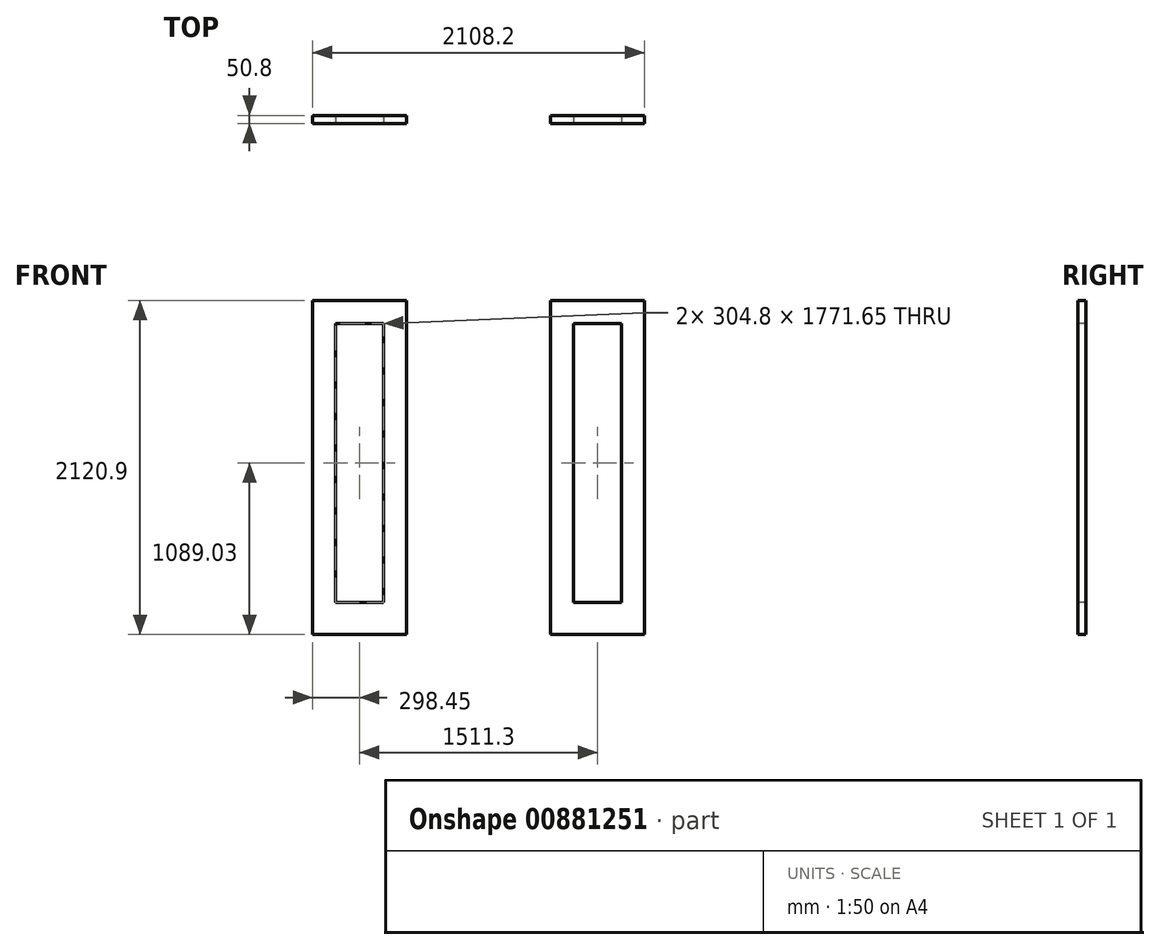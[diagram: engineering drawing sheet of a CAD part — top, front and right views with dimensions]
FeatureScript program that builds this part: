
annotation { "Feature Type Name" : "Feature", "Feature Type Description" : "" }
export const myFeature = defineFeature(function(context is Context, id is Id, definition is map)
    precondition{}
    {
        {
            var Q0;
            Q0=qCreatedBy(makeId("Front.planeOp"),FACE);
            var sketch = newSketch(context, id + "F0", { "sketchPlane" : qUnion([Q0])});
            skLineSegment(sketch, "E0.bottom", {"start": v(-1054.1, 1060.45) * mm, "end": v(1054.1, 1060.45) * mm});
            skLineSegment(sketch, "E0.top", {"start": v(-1054.1, -1060.45) * mm, "end": v(1054.1, -1060.45) * mm});
            skLineSegment(sketch, "E0.left", {"start": v(-1054.1, 1060.45) * mm, "end": v(-1054.1, -1060.45) * mm});
            skLineSegment(sketch, "E0.right", {"start": v(1054.1, 1060.45) * mm, "end": v(1054.1, -1060.45) * mm});
            skSolve(sketch);
        }
        {
            var Q0;
            Q0=qSketchRegion(id+"F0",true);
            extrude(context, id + "F1", {"entities" : qUnion([Q0]), "depth" : 50.8 * mm, "offsetDistance" : 25.4 * mm});
        }
        {
            var Q0;
            Q0=makeQuery(id+"F1.opExtrude","CAP_FACE",FACE,{"disambiguationData":[OSD([sQuery(id+"F0.wireOp",EDGE,"E0.bottom"),sQuery(id+"F0.wireOp",EDGE,"E0.top"),sQuery(id+"F0.wireOp",EDGE,"E0.left"),sQuery(id+"F0.wireOp",EDGE,"E0.right")])],"isStart":false});
            var sketch = newSketch(context, id + "F2", { "sketchPlane" : qUnion([Q0])});
            skLineSegment(sketch, "E1.bottom", {"start": v(-457.2, 1060.45) * mm, "end": v(457.2, 1060.45) * mm});
            skLineSegment(sketch, "E1.top", {"start": v(-457.2, -1060.45) * mm, "end": v(457.2, -1060.45) * mm});
            skLineSegment(sketch, "E1.left", {"start": v(-457.2, 1060.45) * mm, "end": v(-457.2, -1060.45) * mm});
            skLineSegment(sketch, "E1.right", {"start": v(457.2, 1060.45) * mm, "end": v(457.2, -1060.45) * mm});
            skLineSegment(sketch, "E2", {"start": v(-457.2, 0) * mm, "end": v(-1054.1, 0) * mm, "construction": true});
            skLineSegment(sketch, "E3", {"start": v(457.2, 0) * mm, "end": v(1054.1, 0) * mm, "construction": true});
            skSolve(sketch);
        }
        {
            var Q0;
            Q0=qSketchRegion(id+"F2",true);
            extrude(context, id + "F3", {"entities" : qUnion([Q0]), "operationType" : NewBodyOperationType.REMOVE, "oppositeDirection" : true, "depth" : 12.7 * mm, "offsetDistance" : 25.4 * mm});
        }
        {
            var Q0;
            Q0=makeQuery(id+"F3.boolean.opBoolean","COPY",FACE,{"derivedFrom":makeQuery(id+"F3.opExtrude","CAP_FACE",FACE,{"disambiguationData":[OSD([sQuery(id+"F2.wireOp",EDGE,"E1.bottom"),sQuery(id+"F2.wireOp",EDGE,"E1.top"),sQuery(id+"F2.wireOp",EDGE,"E1.left"),sQuery(id+"F2.wireOp",EDGE,"E1.right")])],"isStart":false})});
            var sketch = newSketch(context, id + "F4", { "sketchPlane" : qUnion([Q0])});
            skCircle(sketch, "E4", {"center": v(406.4, 0) * mm, "radius": 25.4 * mm});
            skSolve(sketch);
        }
        {
            var Q0;
            Q0=qSketchRegion(id+"F4",true);
            extrude(context, id + "F5", {"entities" : qUnion([Q0]), "operationType" : NewBodyOperationType.REMOVE, "endBound" : BoundingType.THROUGH_ALL, "oppositeDirection" : true, "depth" : 25.4 * mm, "offsetDistance" : 25.4 * mm});
        }
        {
            var Q0;
            {var subQ0=sQuery(id+"F0.wireOp",EDGE,"E0.bottom");var subQ1=sQuery(id+"F0.wireOp",EDGE,"E0.top");var subQ2=sQuery(id+"F0.wireOp",EDGE,"E0.left");Q0=makeQuery(id+"F3.boolean.opBoolean","SPLIT",FACE,{"disambiguationData":[TD([makeQuery(id+"F1.opExtrude","SWEPT_FACE",FACE,{"disambiguationData":[OSD([subQ2])]})])],"derivedFrom":makeQuery(id+"F1.opExtrude","CAP_FACE",FACE,{"disambiguationData":[OSD([subQ0,subQ1,subQ2,sQuery(id+"F0.wireOp",EDGE,"E0.right")])],"isStart":false})});}
            var sketch = newSketch(context, id + "F6", { "sketchPlane" : qUnion([Q0])});
            skLineSegment(sketch, "E5.bottom", {"start": v(-908.05, 914.4) * mm, "end": v(-603.25, 914.4) * mm});
            skLineSegment(sketch, "E5.top", {"start": v(-908.05, -857.25) * mm, "end": v(-603.25, -857.25) * mm});
            skLineSegment(sketch, "E5.left", {"start": v(-908.05, 914.4) * mm, "end": v(-908.05, -857.25) * mm});
            skLineSegment(sketch, "E5.right", {"start": v(-603.25, 914.4) * mm, "end": v(-603.25, -857.25) * mm});
            skLineSegment(sketch, "E6.bottom", {"start": v(603.25, 914.4) * mm, "end": v(908.05, 914.4) * mm});
            skLineSegment(sketch, "E6.top", {"start": v(603.25, -857.25) * mm, "end": v(908.05, -857.25) * mm});
            skLineSegment(sketch, "E6.left", {"start": v(603.25, 914.4) * mm, "end": v(603.25, -857.25) * mm});
            skLineSegment(sketch, "E6.right", {"start": v(908.05, 914.4) * mm, "end": v(908.05, -857.25) * mm});
            skLineSegment(sketch, "E7", {"start": v(-908.05, 914.4) * mm, "end": v(-1054.1, 914.4) * mm, "construction": true});
            skLineSegment(sketch, "E8", {"start": v(908.05, 914.4) * mm, "end": v(1054.1, 914.4) * mm, "construction": true});
            skLineSegment(sketch, "E9", {"start": v(603.25, 914.4) * mm, "end": v(457.2, 914.4) * mm, "construction": true});
            skLineSegment(sketch, "E10", {"start": v(908.05, 914.4) * mm, "end": v(908.05, 1060.45) * mm, "construction": true});
            skSolve(sketch);
        }
        {
            var Q0;
            Q0=qSketchRegion(id+"F6",true);
            extrude(context, id + "F7", {"entities" : qUnion([Q0]), "operationType" : NewBodyOperationType.REMOVE, "endBound" : BoundingType.THROUGH_ALL, "oppositeDirection" : true, "depth" : 25.4 * mm, "offsetDistance" : 25.4 * mm});
        }
        {
            var Q0;
            Q0=qSketchRegion(id+"F2",true);
            extrude(context, id + "F8", {"entities" : qUnion([Q0]), "operationType" : NewBodyOperationType.REMOVE, "endBound" : BoundingType.THROUGH_ALL, "oppositeDirection" : true, "depth" : 25.4 * mm, "offsetDistance" : 25.4 * mm});
        }
    });
